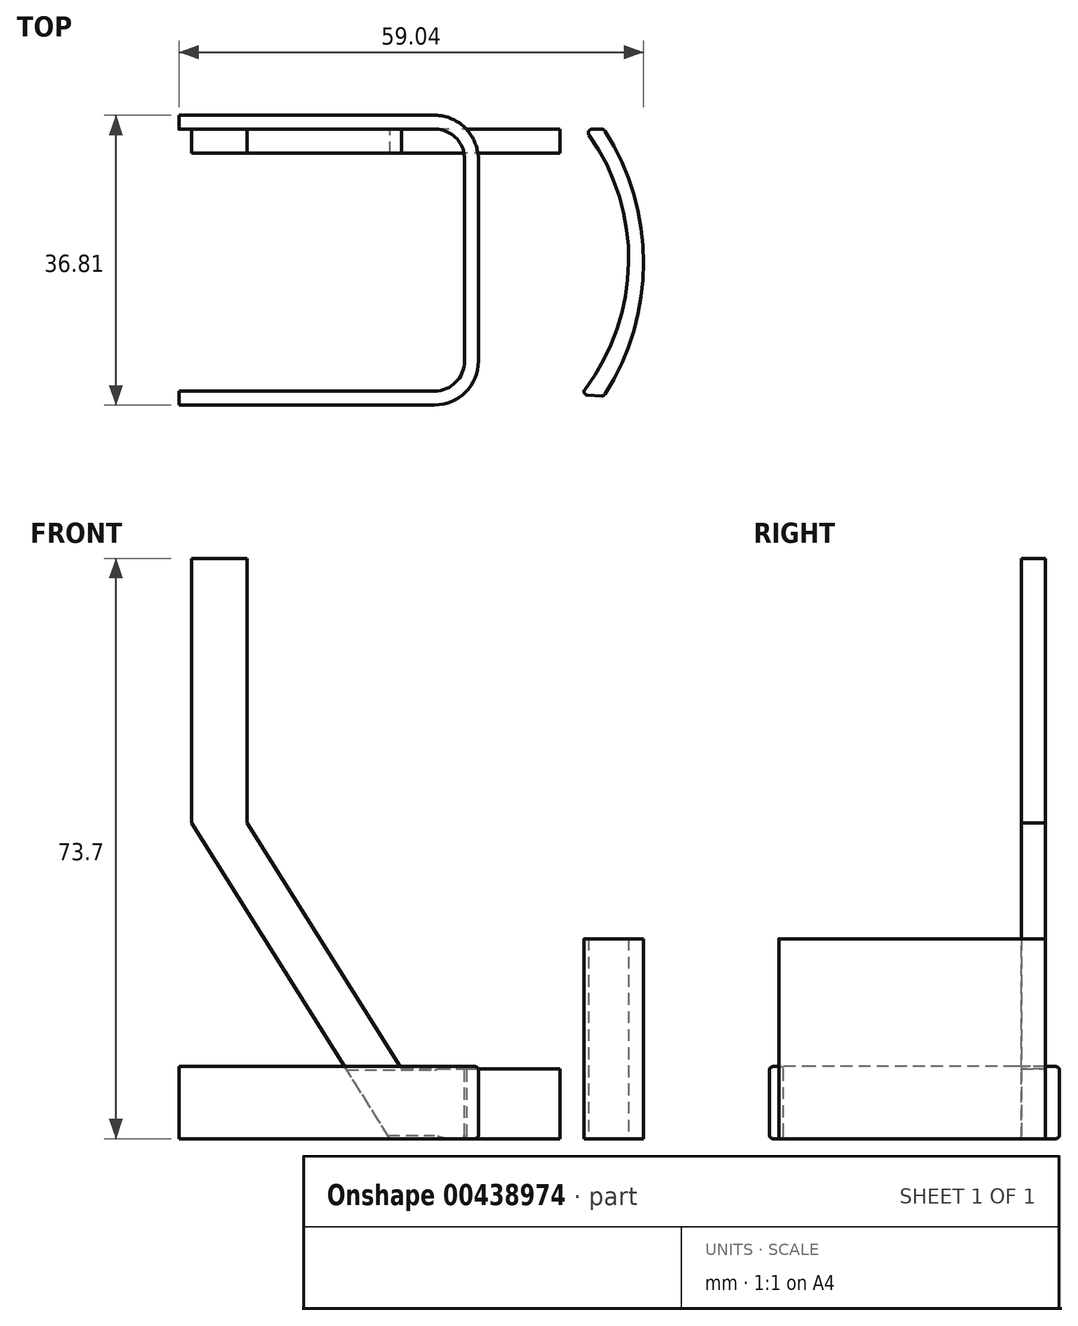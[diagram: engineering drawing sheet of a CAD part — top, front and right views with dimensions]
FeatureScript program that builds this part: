
annotation { "Feature Type Name" : "Feature", "Feature Type Description" : "" }
export const myFeature = defineFeature(function(context is Context, id is Id, definition is map)
    precondition{}
    {
        {
            var Q0;
            Q0=qCreatedBy(makeId("Top.planeOp"),FACE);
            var sketch = newSketch(context, id + "F0", { "sketchPlane" : qUnion([Q0])});
            skLineSegment(sketch, "E0", {"start": v(0, -33.26) * mm, "end": v(32.47, -33.26) * mm});
            skLineSegment(sketch, "E1", {"start": v(36.28, -29.45) * mm, "end": v(36.28, -3.81) * mm});
            skPoint(sketch, "E2.visualSharp", {"position": v(36.28, -33.26) * mm});
            skArc(sketch, "E2.filletArc", {"start": v(32.47, -33.26) * mm, "mid": v(35.17, -32.14) * mm, "end": v(36.28, -29.45) * mm});
            skLineSegment(sketch, "E3", {"start": v(0, 0) * mm, "end": v(32.47, 0) * mm});
            skPoint(sketch, "E4.visualSharp", {"position": v(36.28, 0) * mm});
            skArc(sketch, "E4.filletArc", {"start": v(36.28, -3.81) * mm, "mid": v(35.17, -1.12) * mm, "end": v(32.47, 0) * mm});
            skSolve(sketch);
        }
        {
            var Q0;
            Q0=qCreatedBy(makeId("Right.planeOp"),FACE);
            var sketch = newSketch(context, id + "F1", { "sketchPlane" : qUnion([Q0])});
            skLineSegment(sketch, "E5", {"start": v(0, 0.43) * mm, "end": v(0, 8.73) * mm});
            skLineSegment(sketch, "E6", {"start": v(1.78, 8.73) * mm, "end": v(1.78, 0.43) * mm});
            skLineSegment(sketch, "E7", {"start": v(0.43, 0) * mm, "end": v(1.35, 0) * mm});
            skLineSegment(sketch, "E8", {"start": v(1.35, 9.16) * mm, "end": v(0.43, 9.16) * mm});
            skPoint(sketch, "E9.visualSharp", {"position": v(0, 9.16) * mm});
            skArc(sketch, "E9.filletArc", {"start": v(0.43, 9.16) * mm, "mid": v(0.13, 9.03) * mm, "end": v(0, 8.73) * mm});
            skPoint(sketch, "E10.visualSharp", {"position": v(1.78, 9.16) * mm});
            skArc(sketch, "E10.filletArc", {"start": v(1.78, 8.73) * mm, "mid": v(1.65, 9.03) * mm, "end": v(1.35, 9.16) * mm});
            skPoint(sketch, "E11.visualSharp", {"position": v(1.78, 0) * mm});
            skArc(sketch, "E11.filletArc", {"start": v(1.35, 0) * mm, "mid": v(1.65, 0.13) * mm, "end": v(1.78, 0.43) * mm});
            skPoint(sketch, "E12.visualSharp", {"position": v(0, 0) * mm});
            skArc(sketch, "E12.filletArc", {"start": v(0, 0.43) * mm, "mid": v(0.13, 0.13) * mm, "end": v(0.43, 0) * mm});
            skSolve(sketch);
        }
        {
            var Q0;
            Q0=makeQuery(id+"F1.imprint","IMPRINT",FACE,{"disambiguationData":[TD([[makeQuery(id+"F1.imprint","IMPRINT",EDGE,{"derivedFrom":sQuery(id+"F1.wireOp",EDGE,"E5")}),-1.0]])]});
            var Q1;
            Q1=sQuery(id+"F0.wireOp",EDGE,"E3");
            var Q2;
            Q2=sQuery(id+"F0.wireOp",EDGE,"E4.filletArc");
            var Q3;
            Q3=sQuery(id+"F0.wireOp",EDGE,"E1");
            var Q4;
            Q4=sQuery(id+"F0.wireOp",EDGE,"E2.filletArc");
            var Q5;
            Q5=sQuery(id+"F0.wireOp",EDGE,"E0");
            sweep(context, id + "F2", {"profiles" : qUnion([Q0]), "path" : qUnion([Q1, Q2, Q3, Q4, Q5])});
        }
        {
            var Q0;
            Q0=qCreatedBy(makeId("Top.planeOp"),FACE);
            var sketch = newSketch(context, id + "F3", { "sketchPlane" : qUnion([Q0])});
            skArc(sketch, "E13", {"start": v(54.13, -33.66) * mm, "mid": v(59.04, -16.93) * mm, "end": v(54.13, -0.2) * mm});
            skArc(sketch, "E14", {"start": v(51.57, -33.06) * mm, "mid": v(57.14, -16.97) * mm, "end": v(52.1, -0.72) * mm});
            skLineSegment(sketch, "E15", {"start": v(53.73, -33.87) * mm, "end": v(51.91, -33.78) * mm});
            skLineSegment(sketch, "E16", {"start": v(52.47, 0) * mm, "end": v(53.74, 0) * mm});
            skPoint(sketch, "E17.visualSharp", {"position": v(51.03, -33.74) * mm});
            skArc(sketch, "E17.filletArc", {"start": v(51.57, -33.06) * mm, "mid": v(51.52, -33.52) * mm, "end": v(51.91, -33.78) * mm});
            skPoint(sketch, "E18.visualSharp", {"position": v(54, -33.88) * mm});
            skArc(sketch, "E18.filletArc", {"start": v(53.73, -33.87) * mm, "mid": v(53.96, -33.82) * mm, "end": v(54.13, -33.66) * mm});
            skPoint(sketch, "E19.visualSharp", {"position": v(51.57, 0) * mm});
            skArc(sketch, "E19.filletArc", {"start": v(52.47, 0) * mm, "mid": v(52.06, -0.25) * mm, "end": v(52.1, -0.72) * mm});
            skPoint(sketch, "E20.visualSharp", {"position": v(54, 0) * mm});
            skArc(sketch, "E20.filletArc", {"start": v(54.13, -0.2) * mm, "mid": v(53.96, -0.06) * mm, "end": v(53.74, 0) * mm});
            skSolve(sketch);
        }
        {
            var Q0;
            Q0=qCreatedBy(makeId("Top.planeOp"),FACE);
            var sketch = newSketch(context, id + "F4", { "sketchPlane" : qUnion([Q0])});
            skSolve(sketch);
        }
        {
            var Q0;
            Q0=makeQuery(id+"F3.imprint","IMPRINT",FACE,{"disambiguationData":[TD([[makeQuery(id+"F3.imprint","IMPRINT",EDGE,{"derivedFrom":sQuery(id+"F3.wireOp",EDGE,"E13")}),1.0]])]});
            var Q1;
            Q1=qSketchRegion(id+"F4",true);
            extrude(context, id + "F5", {"entities" : qUnion([Q0, Q1]), "depth" : 25.4 * mm});
        }
        {
            var Q0;
            Q0=qCreatedBy(makeId("Front.planeOp"),FACE);
            var sketch = newSketch(context, id + "F6", { "sketchPlane" : qUnion([Q0])});
            skLineSegment(sketch, "E21", {"start": v(48, 0) * mm, "end": v(26.83, 0) * mm});
            skLineSegment(sketch, "E22", {"start": v(26.83, 0) * mm, "end": v(26.83, 8.9) * mm});
            skLineSegment(sketch, "E23", {"start": v(26.83, 8.9) * mm, "end": v(48.43, 8.9) * mm});
            skLineSegment(sketch, "E24", {"start": v(48.43, 8.9) * mm, "end": v(48.43, 0) * mm});
            skLineSegment(sketch, "E25", {"start": v(48.43, 0) * mm, "end": v(26.83, 0) * mm});
            skLineSegment(sketch, "E26", {"start": v(26.83, 0) * mm, "end": v(1.59, 40.12) * mm});
            skLineSegment(sketch, "E27", {"start": v(1.59, 40.12) * mm, "end": v(8.65, 40.12) * mm});
            skLineSegment(sketch, "E28", {"start": v(8.65, 40.12) * mm, "end": v(33.89, 0) * mm});
            skLineSegment(sketch, "E29", {"start": v(33.89, 0) * mm, "end": v(26.83, 0) * mm});
            skLineSegment(sketch, "E30", {"start": v(1.59, 40.12) * mm, "end": v(1.59, 73.7) * mm});
            skLineSegment(sketch, "E31", {"start": v(1.59, 73.7) * mm, "end": v(8.65, 73.7) * mm});
            skLineSegment(sketch, "E32", {"start": v(8.65, 73.7) * mm, "end": v(8.65, 40.12) * mm});
            skSolve(sketch);
        }
        {
            var Q0;
            {var subQ2=sQuery(id+"F6.wireOp",EDGE,"E22");Q0=makeQuery(id+"F6.imprint","IMPRINT",FACE,{"disambiguationData":[TD([[makeQuery(id+"F6.imprint","IMPRINT",EDGE,{"derivedFrom":subQ2}),1.0]])]});}
            var Q1;
            Q1=makeQuery(id+"F6.imprint","IMPRINT",FACE,{"disambiguationData":[TD([[makeQuery(id+"F6.imprint","IMPRINT",EDGE,{"derivedFrom":sQuery(id+"F6.wireOp",EDGE,"E27")}),1.0]])]});
            var Q2;
            Q2=qSketchRegion(id+"F6",true);
            extrude(context, id + "F7", {"entities" : qUnion([Q0, Q1, Q2]), "operationType" : NewBodyOperationType.ADD, "depth" : 3.05 * mm});
        }
    });
